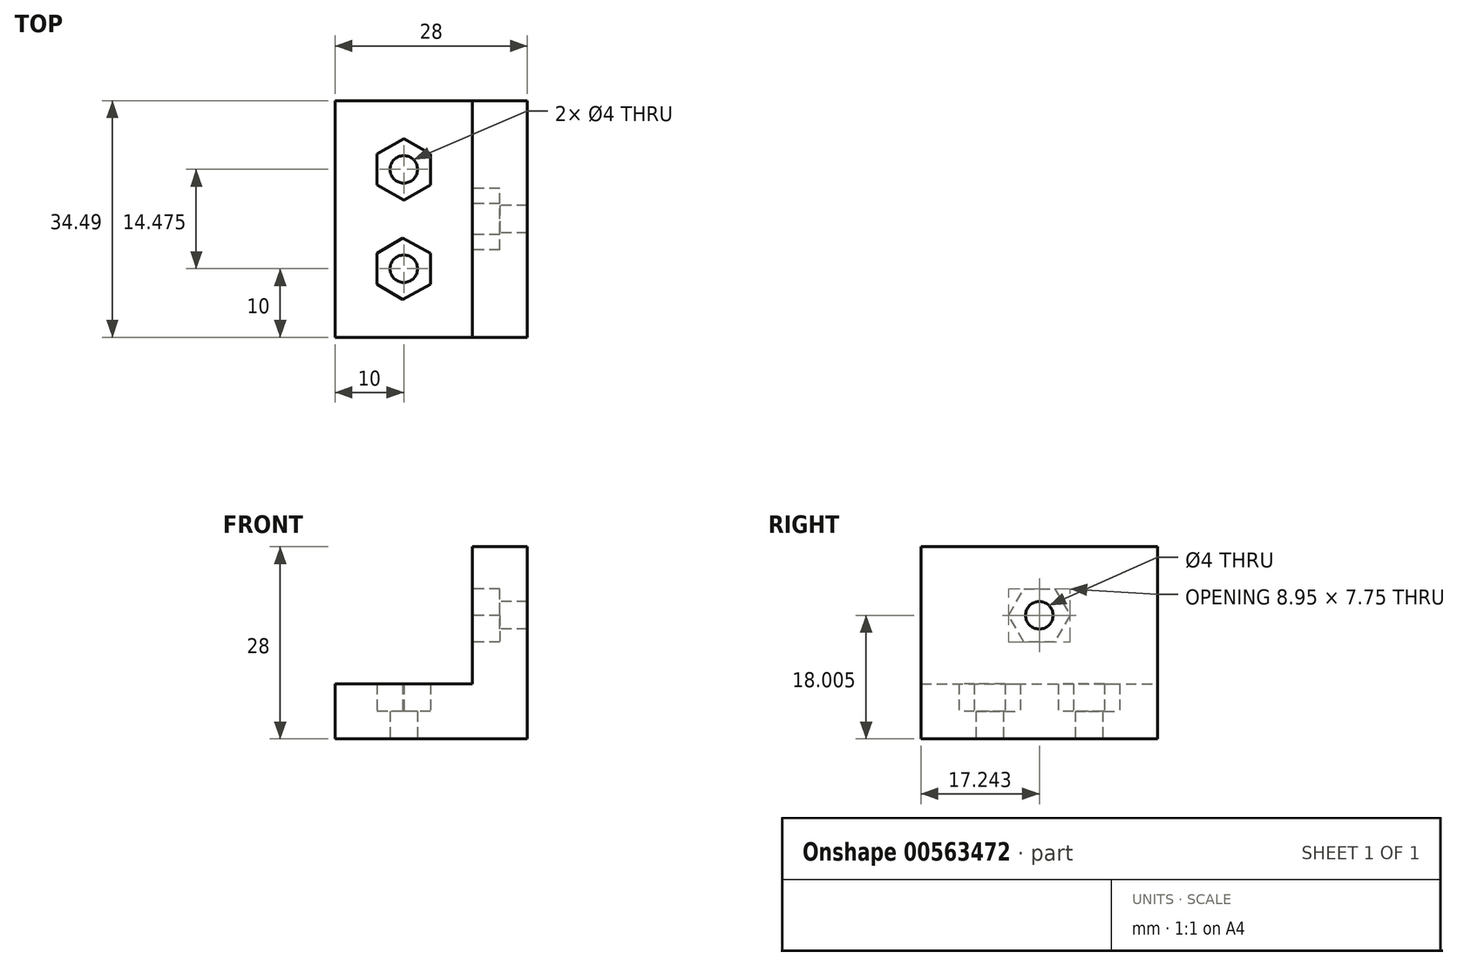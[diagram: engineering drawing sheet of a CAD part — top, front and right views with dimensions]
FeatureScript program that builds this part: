
annotation { "Feature Type Name" : "Feature", "Feature Type Description" : "" }
export const myFeature = defineFeature(function(context is Context, id is Id, definition is map)
    precondition{}
    {
        {
            var Q0;
            Q0=qCreatedBy(makeId("Top.planeOp"),FACE);
            var sketch = newSketch(context, id + "F0", { "sketchPlane" : qUnion([Q0])});
            skLineSegment(sketch, "E0.top", {"start": v(-10, -10) * mm, "end": v(18, -10) * mm});
            skLineSegment(sketch, "E1.0", {"start": v(3.88, 12.24) * mm, "end": v(0, 10) * mm});
            skLineSegment(sketch, "E1.1", {"start": v(0, 10) * mm, "end": v(-3.88, 12.24) * mm});
            skLineSegment(sketch, "E1.2", {"start": v(-3.87, 12.24) * mm, "end": v(-3.87, 16.71) * mm});
            skLineSegment(sketch, "E1.3", {"start": v(-3.87, 16.71) * mm, "end": v(0, 18.95) * mm});
            skLineSegment(sketch, "E1.4", {"start": v(0, 18.95) * mm, "end": v(3.88, 16.71) * mm});
            skLineSegment(sketch, "E1.5", {"start": v(3.88, 16.71) * mm, "end": v(3.88, 12.24) * mm});
            skCircle(sketch, "E2", {"center": v(0, 14.47) * mm, "radius": 2 * mm});
            skLineSegment(sketch, "E3", {"start": v(-10, 24.49) * mm, "end": v(18, 24.49) * mm});
            skLineSegment(sketch, "E4", {"start": v(18, 24.49) * mm, "end": v(18, -10) * mm});
            skLineSegment(sketch, "E5", {"start": v(-10, 24.49) * mm, "end": v(-10, -10) * mm});
            skLineSegment(sketch, "E6.0", {"start": v(3.87, -2.24) * mm, "end": v(-0.14, -4.47) * mm});
            skLineSegment(sketch, "E6.1", {"start": v(-0.14, -4.47) * mm, "end": v(-3.88, -2.24) * mm});
            skLineSegment(sketch, "E6.2", {"start": v(-3.88, -2.24) * mm, "end": v(-3.87, 2.24) * mm});
            skLineSegment(sketch, "E6.3", {"start": v(-3.87, 2.24) * mm, "end": v(-0.14, 4.47) * mm});
            skLineSegment(sketch, "E6.4", {"start": v(-0.14, 4.47) * mm, "end": v(3.88, 2.24) * mm});
            skLineSegment(sketch, "E6.5", {"start": v(3.88, 2.24) * mm, "end": v(3.87, -2.24) * mm});
            skCircle(sketch, "E7", {"center": v(0, 0) * mm, "radius": 2 * mm});
            skSolve(sketch);
        }
        {
            var Q0;
            Q0=makeQuery(id+"F0.imprint","IMPRINT",FACE,{"disambiguationData":[TD([[makeQuery(id+"F0.imprint","IMPRINT",EDGE,{"derivedFrom":sQuery(id+"F0.wireOp",EDGE,"E0.top")}),1.0]])]});
            extrude(context, id + "F1", {"entities" : qUnion([Q0]), "depth" : 8 * mm, "offsetDistance" : 25.4 * mm});
        }
        {
            var Q0;
            Q0=makeQuery(id+"F0.imprint","IMPRINT",FACE,{"disambiguationData":[TD([[makeQuery(id+"F0.imprint","IMPRINT",EDGE,{"derivedFrom":sQuery(id+"F0.wireOp",EDGE,"E1.0")}),-1.0]])]});
            var Q1;
            Q1=makeQuery(id+"F0.imprint","IMPRINT",FACE,{"disambiguationData":[TD([[makeQuery(id+"F0.imprint","IMPRINT",EDGE,{"derivedFrom":sQuery(id+"F0.wireOp",EDGE,"E6.0")}),-1.0]])]});
            extrude(context, id + "F2", {"entities" : qUnion([Q0, Q1]), "operationType" : NewBodyOperationType.ADD, "depth" : 4 * mm, "offsetDistance" : 25.4 * mm});
        }
        {
            var Q0;
            Q0=qCreatedBy(makeId("Right.planeOp"),FACE);
            var sketch = newSketch(context, id + "F3", { "sketchPlane" : qUnion([Q0])});
            skPoint(sketch, "E8.0", {"position": v(-10, 0) * mm});
            skPoint(sketch, "E8.1", {"position": v(24.49, 0) * mm});
            skLineSegment(sketch, "E9", {"start": v(-10, 0) * mm, "end": v(-10, 28) * mm});
            skLineSegment(sketch, "E10", {"start": v(-10, 28) * mm, "end": v(24.49, 28) * mm});
            skLineSegment(sketch, "E11", {"start": v(24.49, 28) * mm, "end": v(24.49, 0) * mm});
            skLineSegment(sketch, "E12", {"start": v(-10, 0) * mm, "end": v(24.49, 0) * mm});
            skLineSegment(sketch, "E13", {"start": v(7.24, 28) * mm, "end": v(7.24, 32) * mm});
            skCircle(sketch, "E14.cCircle", {"center": v(7.24, 18) * mm, "radius": 3.88 * mm, "construction": true});
            skLineSegment(sketch, "E14.0", {"start": v(5, 21.88) * mm, "end": v(9.48, 21.88) * mm});
            skLineSegment(sketch, "E14.1", {"start": v(9.48, 21.88) * mm, "end": v(11.72, 18) * mm});
            skLineSegment(sketch, "E14.2", {"start": v(11.72, 18) * mm, "end": v(9.48, 14.13) * mm});
            skLineSegment(sketch, "E14.3", {"start": v(9.48, 14.13) * mm, "end": v(5, 14.13) * mm});
            skLineSegment(sketch, "E14.4", {"start": v(5, 14.13) * mm, "end": v(2.77, 18) * mm});
            skLineSegment(sketch, "E14.5", {"start": v(2.77, 18) * mm, "end": v(5, 21.88) * mm});
            skPoint(sketch, "E14.0.midPoint", {"position": v(7.24, 21.88) * mm});
            skCircle(sketch, "E15", {"center": v(7.24, 18) * mm, "radius": 2 * mm});
            skSolve(sketch);
        }
        {
            var Q0;
            {var subQ0=sQuery(id+"F3.wireOp",EDGE,"E9");Q0=makeQuery(id+"F3.imprint","IMPRINT",FACE,{"disambiguationData":[TD([[makeQuery(id+"F3.imprint","IMPRINT",EDGE,{"derivedFrom":subQ0}),-1.0]])]});}
            extrude(context, id + "F4", {"entities" : qUnion([Q0]), "operationType" : NewBodyOperationType.ADD, "depth" : 18 * mm, "offsetDistance" : 25.4 * mm, "hasSecondDirection" : true, "secondDirectionOppositeDirection" : false, "secondDirectionDepth" : 10 * mm});
        }
        {
            var Q0;
            Q0=makeQuery(id+"F3.imprint","IMPRINT",FACE,{"disambiguationData":[TD([[makeQuery(id+"F3.imprint","IMPRINT",EDGE,{"derivedFrom":sQuery(id+"F3.wireOp",EDGE,"E14.0")}),-1.0]])]});
            extrude(context, id + "F5", {"entities" : qUnion([Q0]), "operationType" : NewBodyOperationType.ADD, "depth" : 18 * mm, "offsetDistance" : 25.4 * mm, "hasSecondDirection" : true, "secondDirectionOppositeDirection" : false, "secondDirectionDepth" : 14 * mm});
        }
    });
